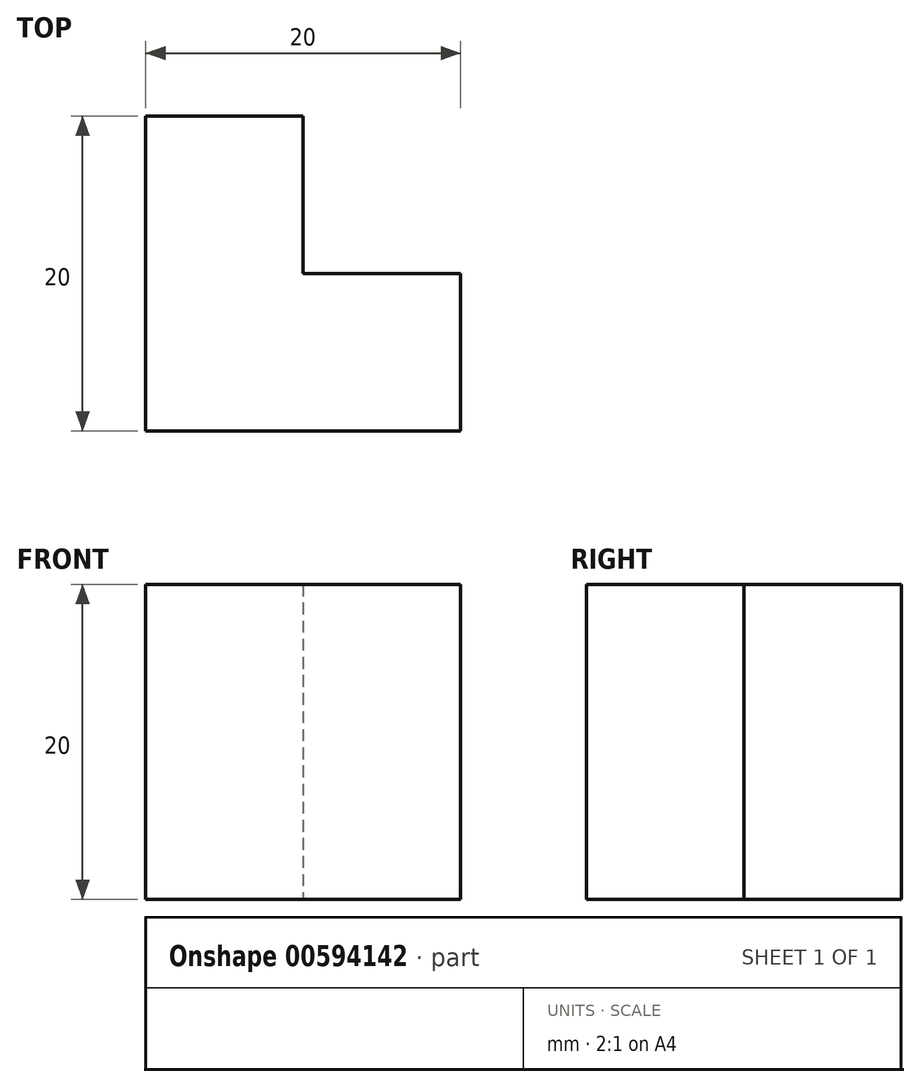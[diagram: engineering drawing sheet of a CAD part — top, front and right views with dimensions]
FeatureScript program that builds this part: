
annotation { "Feature Type Name" : "Feature", "Feature Type Description" : "" }
export const myFeature = defineFeature(function(context is Context, id is Id, definition is map)
    precondition{}
    {
        {
            var Q0;
            Q0=qCreatedBy(makeId("Top.planeOp"),FACE);
            var sketch = newSketch(context, id + "F0", { "sketchPlane" : qUnion([Q0])});
            skLineSegment(sketch, "E0", {"start": v(0, 0) * mm, "end": v(0, 20) * mm});
            skLineSegment(sketch, "E1", {"start": v(0, 20) * mm, "end": v(10, 20) * mm});
            skLineSegment(sketch, "E2", {"start": v(10, 20) * mm, "end": v(10, 10) * mm});
            skLineSegment(sketch, "E3", {"start": v(10, 10) * mm, "end": v(20, 10) * mm});
            skLineSegment(sketch, "E4", {"start": v(20, 10) * mm, "end": v(20, 0) * mm});
            skLineSegment(sketch, "E5", {"start": v(20, 0) * mm, "end": v(0, 0) * mm});
            skSolve(sketch);
        }
        {
            var Q0;
            Q0=makeQuery(id+"F0.imprint","IMPRINT",FACE,{"disambiguationData":[TD([[makeQuery(id+"F0.imprint","IMPRINT",EDGE,{"derivedFrom":sQuery(id+"F0.wireOp",EDGE,"E0")}),-1.0]])]});
            extrude(context, id + "F1", {"entities" : qUnion([Q0]), "depth" : 20 * mm, "offsetDistance" : 25 * mm});
        }
    });
